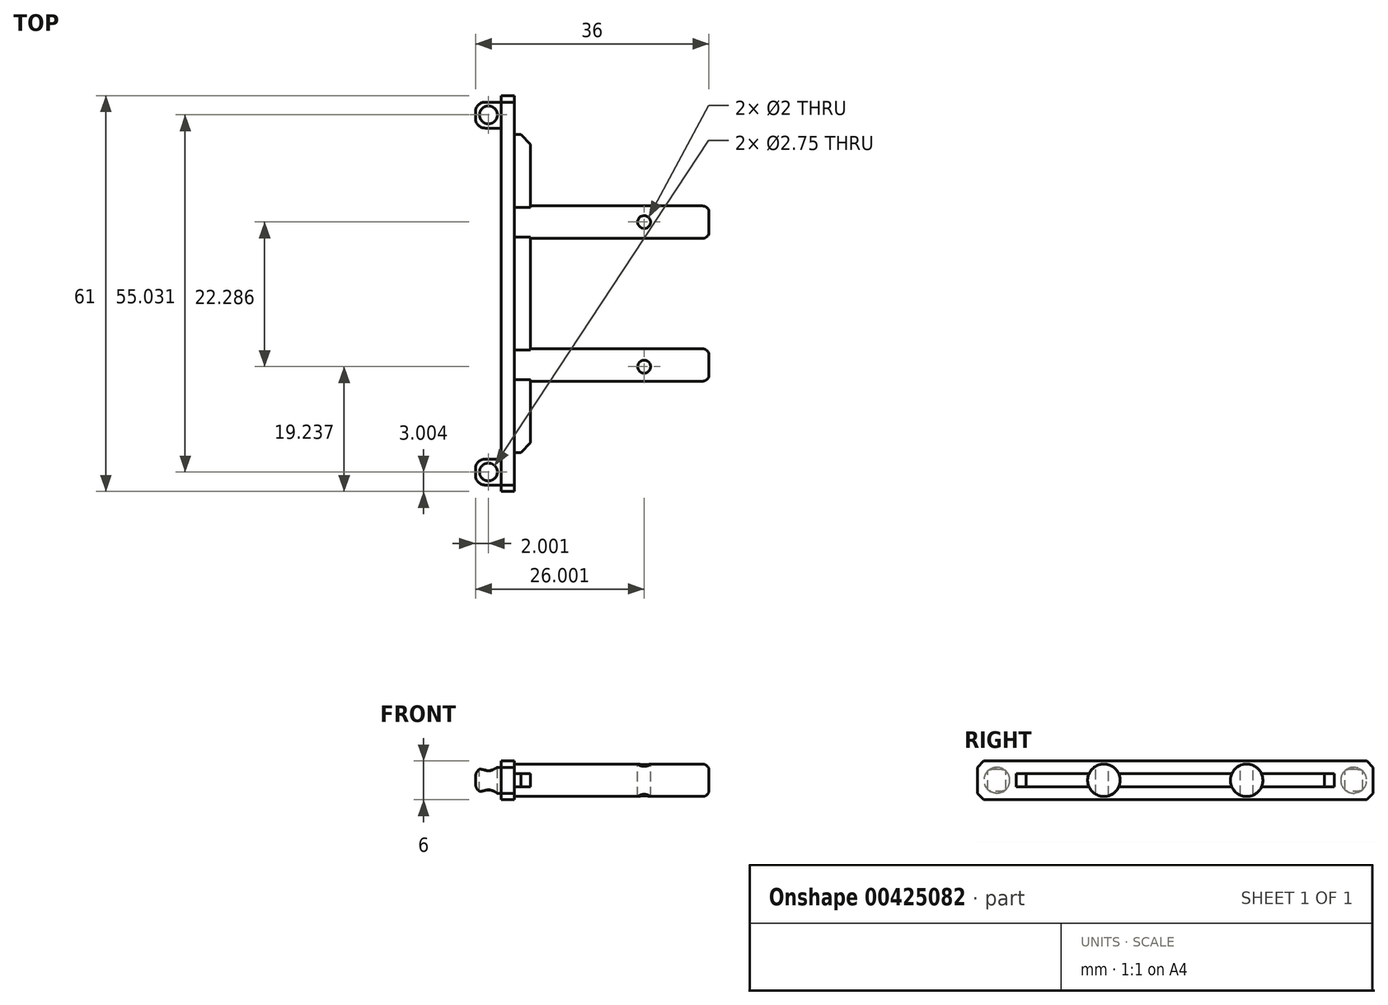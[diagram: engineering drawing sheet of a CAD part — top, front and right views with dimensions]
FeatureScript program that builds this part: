
annotation { "Feature Type Name" : "Feature", "Feature Type Description" : "" }
export const myFeature = defineFeature(function(context is Context, id is Id, definition is map)
    precondition{}
    {
        {
            var Q0;
            Q0=qCreatedBy(makeId("Top.planeOp"),FACE);
            var sketch = newSketch(context, id + "F0", { "sketchPlane" : qUnion([Q0])});
            skLineSegment(sketch, "E0.bottom", {"start": v(-25.84, 48.19) * mm, "end": v(-23.84, 48.19) * mm});
            skLineSegment(sketch, "E0.top", {"start": v(-25.84, -12.81) * mm, "end": v(-23.84, -12.81) * mm});
            skLineSegment(sketch, "E0.left", {"start": v(-25.84, 48.19) * mm, "end": v(-25.84, -12.81) * mm});
            skLineSegment(sketch, "E0.right", {"start": v(-23.84, 48.19) * mm, "end": v(-23.84, -12.81) * mm});
            skLineSegment(sketch, "E1.bottom", {"start": v(-23.84, 42.19) * mm, "end": v(-21.34, 42.19) * mm});
            skLineSegment(sketch, "E1.top", {"start": v(-23.84, -6.81) * mm, "end": v(-21.34, -6.81) * mm});
            skLineSegment(sketch, "E1.left", {"start": v(-23.84, 42.19) * mm, "end": v(-23.84, -6.81) * mm});
            skLineSegment(sketch, "E1.right", {"start": v(-21.34, 42.19) * mm, "end": v(-21.34, -6.81) * mm});
            skSolve(sketch);
        }
        {
            var Q0;
            {var subQ1=sQuery(id+"F0.wireOp",EDGE,"E0.bottom");Q0=makeQuery(id+"F0.imprint","IMPRINT",FACE,{"disambiguationData":[TD([[makeQuery(id+"F0.imprint","IMPRINT",EDGE,{"derivedFrom":subQ1}),-1.0]])]});}
            extrude(context, id + "F1", {"entities" : qUnion([Q0]), "endBound" : BoundingType.SYMMETRIC, "depth" : 6 * mm});
        }
        {
            var Q0;
            Q0=makeQuery(id+"F1.opExtrude","SWEPT_FACE",FACE,{"disambiguationData":[OSD([sQuery(id+"F0.wireOp",EDGE,"E0.left")])]});
            var sketch = newSketch(context, id + "F2", { "sketchPlane" : qUnion([Q0])});
            skCircle(sketch, "E2", {"center": v(-45.19, 0) * mm, "radius": 2 * mm});
            skCircle(sketch, "E3", {"center": v(9.81, 0) * mm, "radius": 2 * mm});
            skSolve(sketch);
        }
        {
            var Q0;
            Q0=makeQuery(id+"F2.imprint","IMPRINT",FACE,{"disambiguationData":[TD([[makeQuery(id+"F2.imprint","IMPRINT",EDGE,{"derivedFrom":sQuery(id+"F2.wireOp",EDGE,"E2")}),1.0]])]});
            var Q1;
            Q1=makeQuery(id+"F2.imprint","IMPRINT",FACE,{"disambiguationData":[TD([[makeQuery(id+"F2.imprint","IMPRINT",EDGE,{"derivedFrom":sQuery(id+"F2.wireOp",EDGE,"E3")}),1.0]])]});
            extrude(context, id + "F3", {"entities" : qUnion([Q0, Q1]), "operationType" : NewBodyOperationType.ADD, "depth" : 4 * mm});
        }
        {
            var Q0;
            Q0=makeQuery(id+"F1.opExtrude","SWEPT_FACE",FACE,{"disambiguationData":[OSD([sQuery(id+"F0.wireOp",EDGE,"E0.right")])]});
            var sketch = newSketch(context, id + "F4", { "sketchPlane" : qUnion([Q0])});
            skCircle(sketch, "E4", {"center": v(28.69, 0) * mm, "radius": 2.5 * mm});
            skCircle(sketch, "E5", {"center": v(6.69, 0) * mm, "radius": 2.5 * mm});
            skSolve(sketch);
        }
        {
            var Q0;
            Q0=makeQuery(id+"F4.imprint","IMPRINT",FACE,{"disambiguationData":[TD([[makeQuery(id+"F4.imprint","IMPRINT",EDGE,{"derivedFrom":sQuery(id+"F4.wireOp",EDGE,"E4")}),1.0]])]});
            var Q1;
            Q1=makeQuery(id+"F4.imprint","IMPRINT",FACE,{"disambiguationData":[TD([[makeQuery(id+"F4.imprint","IMPRINT",EDGE,{"derivedFrom":sQuery(id+"F4.wireOp",EDGE,"E5")}),1.0]])]});
            extrude(context, id + "F5", {"entities" : qUnion([Q0, Q1]), "operationType" : NewBodyOperationType.ADD, "depth" : 30 * mm});
        }
        {
            var Q0;
            Q0=makeQuery(id+"F0.imprint","IMPRINT",FACE,{"disambiguationData":[TD([[makeQuery(id+"F0.imprint","IMPRINT",EDGE,{"derivedFrom":sQuery(id+"F0.wireOp",EDGE,"E1.bottom")}),-1.0]])]});
            extrude(context, id + "F6", {"entities" : qUnion([Q0]), "operationType" : NewBodyOperationType.ADD, "endBound" : BoundingType.SYMMETRIC, "depth" : 2 * mm});
        }
        {
            var Q0;
            Q0=makeQuery(id+"F6.opExtrude","SWEPT_EDGE",EDGE,{"disambiguationData":[OSD([sQuery(id+"F0.wireOp",EDGE,"E1.bottom"),sQuery(id+"F0.wireOp",EDGE,"E1.right")])]});
            var Q1;
            Q1=makeQuery(id+"F6.opExtrude","SWEPT_EDGE",EDGE,{"disambiguationData":[OSD([sQuery(id+"F0.wireOp",EDGE,"E1.top"),sQuery(id+"F0.wireOp",EDGE,"E1.right")])]});
            chamfer(context, id + "F7", {"entities" : qUnion([Q0, Q1]), "width" : 1.5 * mm, "tangentPropagation" : true});
        }
        {
            var Q0;
            Q0=makeQuery(id+"F1.opExtrude","CAP_EDGE",EDGE,{"disambiguationData":[OSD([sQuery(id+"F0.wireOp",EDGE,"E0.top")])],"isStart":false});
            var Q1;
            Q1=makeQuery(id+"F1.opExtrude","CAP_EDGE",EDGE,{"disambiguationData":[OSD([sQuery(id+"F0.wireOp",EDGE,"E0.top")])],"isStart":true});
            var Q2;
            Q2=makeQuery(id+"F1.opExtrude","CAP_EDGE",EDGE,{"disambiguationData":[OSD([sQuery(id+"F0.wireOp",EDGE,"E0.bottom")])],"isStart":false});
            var Q3;
            Q3=makeQuery(id+"F1.opExtrude","CAP_EDGE",EDGE,{"disambiguationData":[OSD([sQuery(id+"F0.wireOp",EDGE,"E0.bottom")])],"isStart":true});
            chamfer(context, id + "F8", {"entities" : qUnion([Q0, Q1, Q2, Q3]), "width" : 1 * mm, "tangentPropagation" : true});
        }
        {
            var Q0;
            Q0=makeQuery(id+"F5.opExtrude","CAP_FACE",FACE,{"disambiguationData":[OSD([sQuery(id+"F4.wireOp",EDGE,"E5")])],"isStart":false});
            var Q1;
            Q1=makeQuery(id+"F5.opExtrude","CAP_FACE",FACE,{"disambiguationData":[OSD([sQuery(id+"F4.wireOp",EDGE,"E4")])],"isStart":false});
            fillet(context, id + "F9", {"entities" : qUnion([Q0, Q1]), "radius" : 1 * mm, "allowEdgeOverflow" : false});
        }
        {
            var Q0;
            Q0=makeQuery(id+"F3.opExtrude","CAP_FACE",FACE,{"disambiguationData":[OSD([sQuery(id+"F2.wireOp",EDGE,"E3")])],"isStart":false});
            var Q1;
            Q1=makeQuery(id+"F3.opExtrude","CAP_FACE",FACE,{"disambiguationData":[OSD([sQuery(id+"F2.wireOp",EDGE,"E2")])],"isStart":false});
            fillet(context, id + "F10", {"entities" : qUnion([Q0, Q1]), "radius" : 1.5 * mm, "tangentPropagation" : true, "allowEdgeOverflow" : false});
        }
        {
            var Q0;
            Q0=qCreatedBy(makeId("Top.planeOp"),FACE);
            var sketch = newSketch(context, id + "F11", { "sketchPlane" : qUnion([Q0])});
            skPoint(sketch, "E6", {"position": v(-27.84, -9.8) * mm});
            skPoint(sketch, "E7", {"position": v(-27.84, 45.23) * mm});
            skPoint(sketch, "E8", {"position": v(-3.84, 28.71) * mm});
            skPoint(sketch, "E9", {"position": v(-3.84, 6.43) * mm});
            skSolve(sketch);
        }
        {
            var Q0;
            Q0=sQuery(id+"F11.wireOp",VERTEX,"E8");
            var Q1;
            Q1=sQuery(id+"F11.wireOp",VERTEX,"E9");
            var Q2;
            Q2=makeQuery(id+"F1.opExtrude","SWEPT_BODY",BODY,{"disambiguationData":[OSD([sQuery(id+"F0.wireOp",EDGE,"E0.bottom"),sQuery(id+"F0.wireOp",EDGE,"E0.top"),sQuery(id+"F0.wireOp",EDGE,"E0.left"),sQuery(id+"F0.wireOp",EDGE,"E0.right"),sQuery(id+"F0.wireOp",EDGE,"E1.left")])]});
            hole(context, id + "F12", {"style" : HoleStyle.SIMPLE, "endStyle" : HoleEndStyle.THROUGH, "holeDiameter" : 2 * mm, "isTappedThrough" : true, "tappedDepth" : 12 * mm, "tapClearance" : 3, "startFromSketch" : true, "locations" : qUnion([Q0, Q1]), "scope" : qUnion([Q2])});
        }
        {
            var Q0;
            Q0=sQuery(id+"F11.wireOp",VERTEX,"E8");
            var Q1;
            Q1=sQuery(id+"F11.wireOp",VERTEX,"E9");
            var Q2;
            Q2=makeQuery(id+"F1.opExtrude","SWEPT_BODY",BODY,{"disambiguationData":[OSD([sQuery(id+"F0.wireOp",EDGE,"E0.bottom"),sQuery(id+"F0.wireOp",EDGE,"E0.top"),sQuery(id+"F0.wireOp",EDGE,"E0.left"),sQuery(id+"F0.wireOp",EDGE,"E0.right"),sQuery(id+"F0.wireOp",EDGE,"E1.left")])]});
            hole(context, id + "F13", {"style" : HoleStyle.SIMPLE, "endStyle" : HoleEndStyle.THROUGH, "oppositeDirection" : true, "holeDiameter" : 2 * mm, "isTappedThrough" : true, "tappedDepth" : 12 * mm, "tapClearance" : 3, "startFromSketch" : true, "locations" : qUnion([Q0, Q1]), "scope" : qUnion([Q2])});
        }
        {
            var Q0;
            Q0=sQuery(id+"F11.wireOp",VERTEX,"E7");
            var Q1;
            Q1=sQuery(id+"F11.wireOp",VERTEX,"E6");
            var Q2;
            Q2=makeQuery(id+"F1.opExtrude","SWEPT_BODY",BODY,{"disambiguationData":[OSD([sQuery(id+"F0.wireOp",EDGE,"E0.bottom"),sQuery(id+"F0.wireOp",EDGE,"E0.top"),sQuery(id+"F0.wireOp",EDGE,"E0.left"),sQuery(id+"F0.wireOp",EDGE,"E0.right"),sQuery(id+"F0.wireOp",EDGE,"E1.left")])]});
            hole(context, id + "F14", {"style" : HoleStyle.SIMPLE, "endStyle" : HoleEndStyle.THROUGH, "holeDiameter" : 2.75 * mm, "isTappedThrough" : true, "tappedDepth" : 12 * mm, "tapClearance" : 3, "startFromSketch" : true, "locations" : qUnion([Q0, Q1]), "scope" : qUnion([Q2])});
        }
        {
            var Q0;
            Q0=sQuery(id+"F11.wireOp",VERTEX,"E7");
            var Q1;
            Q1=sQuery(id+"F11.wireOp",VERTEX,"E6");
            var Q2;
            Q2=makeQuery(id+"F1.opExtrude","SWEPT_BODY",BODY,{"disambiguationData":[OSD([sQuery(id+"F0.wireOp",EDGE,"E0.bottom"),sQuery(id+"F0.wireOp",EDGE,"E0.top"),sQuery(id+"F0.wireOp",EDGE,"E0.left"),sQuery(id+"F0.wireOp",EDGE,"E0.right"),sQuery(id+"F0.wireOp",EDGE,"E1.left")])]});
            hole(context, id + "F15", {"style" : HoleStyle.SIMPLE, "endStyle" : HoleEndStyle.THROUGH, "oppositeDirection" : true, "holeDiameter" : 2.75 * mm, "isTappedThrough" : true, "tappedDepth" : 12 * mm, "tapClearance" : 3, "startFromSketch" : true, "locations" : qUnion([Q0, Q1]), "scope" : qUnion([Q2])});
        }
    });
